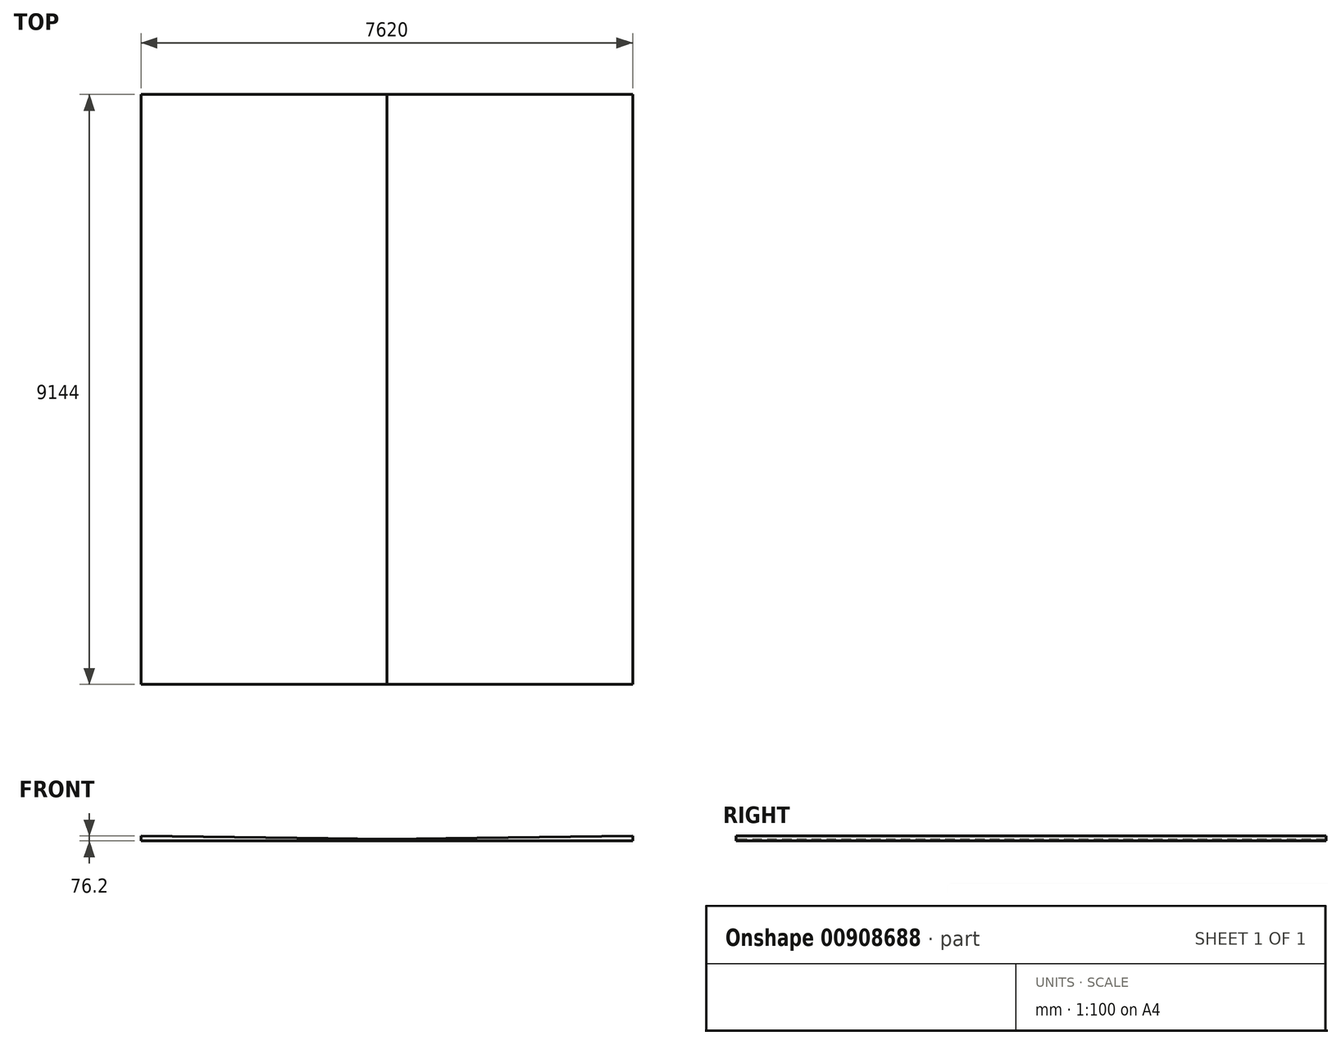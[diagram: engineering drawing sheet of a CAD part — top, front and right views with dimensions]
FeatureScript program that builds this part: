
annotation { "Feature Type Name" : "Feature", "Feature Type Description" : "" }
export const myFeature = defineFeature(function(context is Context, id is Id, definition is map)
    precondition{}
    {
        {
            var Q0;
            Q0=qCreatedBy(makeId("Top.planeOp"),FACE);
            var sketch = newSketch(context, id + "F0", { "sketchPlane" : qUnion([Q0])});
            skLineSegment(sketch, "E0.bottom", {"start": v(3810, 4572) * mm, "end": v(-3810, 4572) * mm});
            skLineSegment(sketch, "E0.top", {"start": v(3810, -4572) * mm, "end": v(-3810, -4572) * mm});
            skLineSegment(sketch, "E0.left", {"start": v(3810, 4572) * mm, "end": v(3810, -4572) * mm});
            skLineSegment(sketch, "E0.right", {"start": v(-3810, 4572) * mm, "end": v(-3810, -4572) * mm});
            skPoint(sketch, "E0.middle", {"position": v(0, 0) * mm});
            skSolve(sketch);
        }
        {
            var Q0;
            Q0=makeQuery(id+"F0.imprint","IMPRINT",FACE,{"disambiguationData":[TD([[makeQuery(id+"F0.imprint","IMPRINT",EDGE,{"derivedFrom":sQuery(id+"F0.wireOp",EDGE,"E0.bottom")}),1.0]])]});
            extrude(context, id + "F1", {"entities" : qUnion([Q0]), "depth" : 76.2 * mm, "offsetDistance" : 25.4 * mm});
        }
        {
            var Q0;
            Q0=makeQuery(id+"F1.opExtrude","SWEPT_FACE",FACE,{"disambiguationData":[OSD([sQuery(id+"F0.wireOp",EDGE,"E0.top")])]});
            var sketch = newSketch(context, id + "F2", { "sketchPlane" : qUnion([Q0])});
            skLineSegment(sketch, "E1.0", {"start": v(3810, 0) * mm, "end": v(-3810, 0) * mm});
            skLineSegment(sketch, "E2.0", {"start": v(3810, 76.2) * mm, "end": v(-3810, 76.2) * mm, "construction": true});
            skPoint(sketch, "E3.0", {"position": v(-3810, 38.1) * mm});
            skLineSegment(sketch, "E4.0", {"start": v(-3810, 76.2) * mm, "end": v(-3810, 0) * mm});
            skLineSegment(sketch, "E5.0", {"start": v(3810, 76.2) * mm, "end": v(3810, 0) * mm});
            skLineSegment(sketch, "E6.0", {"start": v(914.4, 0) * mm, "end": v(914.4, 76.2) * mm, "construction": true});
            skLineSegment(sketch, "E7.0", {"start": v(-914.4, 0) * mm, "end": v(-914.4, 76.2) * mm, "construction": true});
            skLineSegment(sketch, "E8", {"start": v(-3810, 76.2) * mm, "end": v(-914.4, 38.1) * mm});
            skLineSegment(sketch, "E9", {"start": v(0, 0) * mm, "end": v(0, 25.4) * mm, "construction": true});
            skLineSegment(sketch, "E10", {"start": v(-914.4, 38.1) * mm, "end": v(0, 25.4) * mm});
            skLineSegment(sketch, "E11", {"start": v(0, 25.4) * mm, "end": v(914.4, 38.1) * mm});
            skLineSegment(sketch, "E12", {"start": v(914.4, 38.1) * mm, "end": v(3810, 76.2) * mm});
            skSolve(sketch);
        }
        {
            var Q0;
            Q0=makeQuery(id+"F2.imprint","IMPRINT",FACE,{"disambiguationData":[TD([[makeQuery(id+"F2.imprint","IMPRINT",EDGE,{"derivedFrom":sQuery(id+"F2.wireOp",EDGE,"E8")}),1.0]])]});
            var Q1;
            Q1=makeQuery(id+"F1.opExtrude","SWEPT_FACE",FACE,{"disambiguationData":[OSD([sQuery(id+"F0.wireOp",EDGE,"E0.bottom")])]});
            extrude(context, id + "F3", {"entities" : qUnion([Q0]), "operationType" : NewBodyOperationType.REMOVE, "endBound" : BoundingType.UP_TO_SURFACE, "oppositeDirection" : true, "depth" : 25.4 * mm, "endBoundEntityFace" : qUnion([Q1]), "offsetDistance" : 25.4 * mm});
        }
    });
